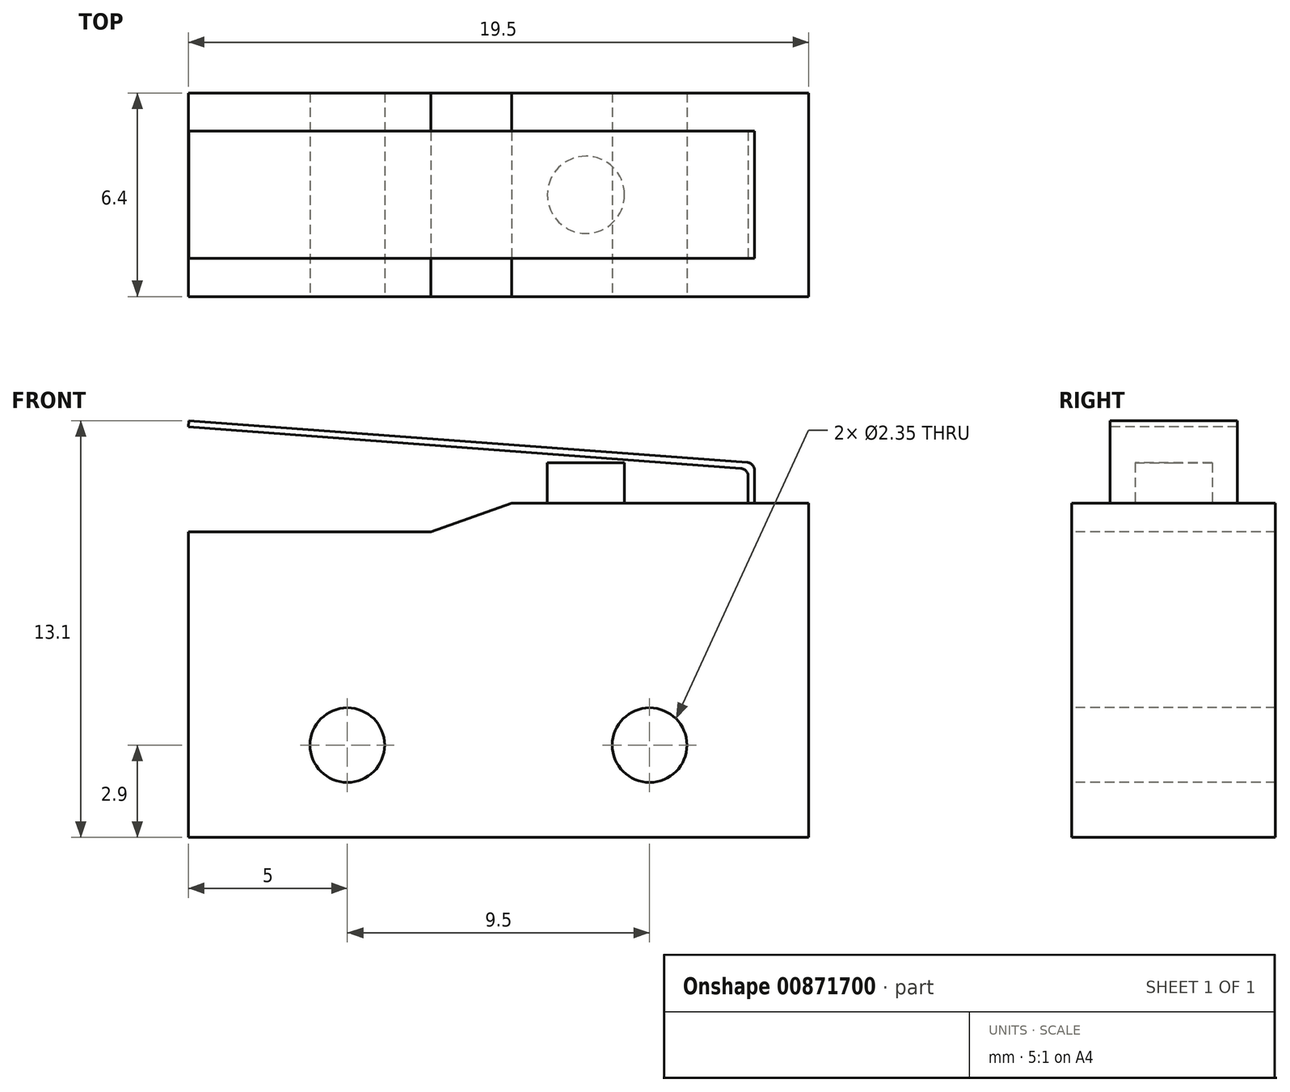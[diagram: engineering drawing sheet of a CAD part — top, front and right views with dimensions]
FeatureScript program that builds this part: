
annotation { "Feature Type Name" : "Feature", "Feature Type Description" : "" }
export const myFeature = defineFeature(function(context is Context, id is Id, definition is map)
    precondition{}
    {
        {
            var Q0;
            Q0=qCreatedBy(makeId("Front.planeOp"),FACE);
            var sketch = newSketch(context, id + "F0", { "sketchPlane" : qUnion([Q0])});
            skLineSegment(sketch, "E0.bottom", {"start": v(0, 0) * mm, "end": v(19.5, 0) * mm});
            skLineSegment(sketch, "E0.top", {"start": v(0, 10.5) * mm, "end": v(19.5, 10.5) * mm});
            skLineSegment(sketch, "E0.left", {"start": v(0, 0) * mm, "end": v(0, 10.5) * mm});
            skLineSegment(sketch, "E0.right", {"start": v(19.5, 0) * mm, "end": v(19.5, 10.5) * mm});
            skSolve(sketch);
        }
        {
            var Q0;
            Q0 = qSketchRegion(id + "F0", true);
            extrude(context, id + "F1", {"entities" : qUnion([Q0]), "depth" : 6.4 * mm, "offsetDistance" : 25.4 * mm});
        }
        {
            var Q0;
            Q0=makeQuery(id+"F1.opExtrude","CAP_FACE",FACE,{"disambiguationData":[OSD([sQuery(id+"F0.wireOp",EDGE,"E0.bottom"),sQuery(id+"F0.wireOp",EDGE,"E0.top"),sQuery(id+"F0.wireOp",EDGE,"E0.left"),sQuery(id+"F0.wireOp",EDGE,"E0.right")])],"isStart":false});
            var sketch = newSketch(context, id + "F2", { "sketchPlane" : qUnion([Q0])});
            skCircle(sketch, "E1", {"center": v(5, 2.9) * mm, "radius": 1.17 * mm});
            skCircle(sketch, "E2", {"center": v(14.5, 2.9) * mm, "radius": 1.17 * mm});
            skSolve(sketch);
        }
        {
            var Q0;
            Q0 = qSketchRegion(id + "F2", true);
            extrude(context, id + "F3", {"entities" : qUnion([Q0]), "operationType" : NewBodyOperationType.REMOVE, "oppositeDirection" : true, "depth" : 25.4 * mm, "offsetDistance" : 25.4 * mm});
        }
        {
            var Q0;
            Q0=makeQuery(id+"F1.opExtrude","CAP_FACE",FACE,{"disambiguationData":[OSD([sQuery(id+"F0.wireOp",EDGE,"E0.bottom"),sQuery(id+"F0.wireOp",EDGE,"E0.top"),sQuery(id+"F0.wireOp",EDGE,"E0.left"),sQuery(id+"F0.wireOp",EDGE,"E0.right")])],"isStart":false});
            var sketch = newSketch(context, id + "F4", { "sketchPlane" : qUnion([Q0])});
            skLineSegment(sketch, "E3", {"start": v(0, 10.5) * mm, "end": v(10.16, 10.5) * mm});
            skLineSegment(sketch, "E4", {"start": v(10.16, 10.5) * mm, "end": v(7.62, 9.6) * mm});
            skLineSegment(sketch, "E5", {"start": v(7.62, 9.6) * mm, "end": v(0, 9.6) * mm});
            skPoint(sketch, "E5.endSnap0", {"position": v(0, 5.25) * mm});
            skLineSegment(sketch, "E6", {"start": v(0, 9.6) * mm, "end": v(0, 10.5) * mm});
            skSolve(sketch);
        }
        {
            var Q0;
            Q0 = qSketchRegion(id + "F4", true);
            extrude(context, id + "F5", {"entities" : qUnion([Q0]), "operationType" : NewBodyOperationType.REMOVE, "oppositeDirection" : true, "depth" : 25.4 * mm, "offsetDistance" : 25.4 * mm});
        }
        {
            var Q0;
            Q0=makeQuery(id+"F1.opExtrude","SWEPT_FACE",FACE,{"disambiguationData":[OSD([sQuery(id+"F0.wireOp",EDGE,"E0.top")])]});
            var sketch = newSketch(context, id + "F6", { "sketchPlane" : qUnion([Q0])});
            skCircle(sketch, "E7", {"center": v(12.5, -3.2) * mm, "radius": 1.21 * mm});
            skSolve(sketch);
        }
        {
            var Q0;
            Q0 = qSketchRegion(id + "F6", true);
            extrude(context, id + "F7", {"entities" : qUnion([Q0]), "operationType" : NewBodyOperationType.ADD, "depth" : 1.27 * mm, "offsetDistance" : 25.4 * mm});
        }
        {
            var Q0;
            Q0=makeQuery(id+"F1.opExtrude","CAP_FACE",FACE,{"disambiguationData":[OSD([sQuery(id+"F0.wireOp",EDGE,"E0.bottom"),sQuery(id+"F0.wireOp",EDGE,"E0.top"),sQuery(id+"F0.wireOp",EDGE,"E0.left"),sQuery(id+"F0.wireOp",EDGE,"E0.right")])],"isStart":false});
            cPlane(context, id + "F8", {"entities" : qUnion([Q0]), "cplaneType" : CPlaneType.OFFSET, "offset" : 1.2 * mm, "oppositeDirection" : true, "width" : 152.4 * mm, "height" : 152.4 * mm});
        }
        {
            var Q0;
            Q0=qCreatedBy(id+"F8.planeOp",FACE);
            var sketch = newSketch(context, id + "F9", { "sketchPlane" : qUnion([Q0])});
            skLineSegment(sketch, "E8", {"start": v(17.6, 10.5) * mm, "end": v(17.6, 11.58) * mm});
            skLineSegment(sketch, "E9", {"start": v(17.6, 11.58) * mm, "end": v(0, 12.9) * mm});
            skLineSegment(sketch, "E10", {"start": v(0, 12.9) * mm, "end": v(0.01, 13.1) * mm});
            skLineSegment(sketch, "E11", {"start": v(0.01, 13.1) * mm, "end": v(17.8, 11.77) * mm});
            skLineSegment(sketch, "E12", {"start": v(17.8, 11.77) * mm, "end": v(17.8, 10.5) * mm});
            skLineSegment(sketch, "E13", {"start": v(17.8, 10.5) * mm, "end": v(17.6, 10.5) * mm});
            skLineSegment(sketch, "E14", {"start": v(0, 8.64) * mm, "end": v(0, 12.66) * mm, "construction": true});
            skSolve(sketch);
        }
        {
            var Q0;
            Q0 = qSketchRegion(id + "F9", true);
            extrude(context, id + "F10", {"entities" : qUnion([Q0]), "operationType" : NewBodyOperationType.ADD, "oppositeDirection" : true, "depth" : 4 * mm, "offsetDistance" : 25.4 * mm});
        }
        {
            var Q0;
            Q0=makeQuery(id+"F10.opExtrude","SWEPT_EDGE",EDGE,{"disambiguationData":[OSD([sQuery(id+"F9.wireOp",EDGE,"E11"),sQuery(id+"F9.wireOp",EDGE,"E12")])]});
            var Q1;
            Q1=makeQuery(id+"F10.opExtrude","SWEPT_EDGE",EDGE,{"disambiguationData":[OSD([sQuery(id+"F9.wireOp",EDGE,"E8"),sQuery(id+"F9.wireOp",EDGE,"E9")])]});
            fillet(context, id + "F11", {"entities" : qUnion([Q0, Q1]), "radius" : 0.25 * mm, "tangentPropagation" : true, "allowEdgeOverflow" : false});
        }
    });
